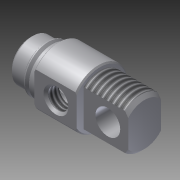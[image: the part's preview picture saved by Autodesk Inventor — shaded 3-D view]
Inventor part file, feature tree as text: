
AUTODESK INVENTOR PART (.ipt)
format: ipt  version: 2012 (Build 160160000, 160)  size: 246,784 bytes
history: native  units: in
note: dims shown in document units (in); Inventor stores cm internally (conversion verified against a paired STEP export)
features: other x126, sketch x8, revolve x3, extrude x3, hole x2, thread x1
ambient origin geometry x8: Origin, YZ Plane, XZ Plane, XY Plane, X Axis, Y Axis, Z Axis, Center Point
bodies: Solid1 (feature_tree)
feature tree (143):
  revolve  "Revolution1"  Angle=360.0deg
  revolve  "Revolution2"  [1 undecoded]
  thread  "Thread1"  [1 undecoded]
  extrude  "Extrusion1"  TaperAngle=360.0deg  [1 undecoded]
  extrude  "Extrusion2"  [1 undecoded]
  hole  "Drilling 1"  [1 undecoded]
  hole  "Drilling 2"  [1 undecoded]
  revolve  "Revolution3"  [1 undecoded]
  extrude  "Extrusion3"  [1 undecoded]
  other  "to_tube_XY"
  other  "to_tube_YZ"
  other  "to_tube_ZX"
  other  "to_tube_X"
  other  "to_tube_Y"
  other  "to_tube_Z"
  other  "to_tube_Center"
  other  "to_nut_XY"
  other  "to_nut_YZ"
  other  "to_nut_ZX"
  other  "to_nut_X"
  other  "to_nut_Y"
  other  "to_nut_Z"
  other  "to_nut_Center"
  other  "lovra1_XY"
  other  "lovra1_YZ"
  other  "lovra1_ZX"
  other  "lovra1_X"
  other  "lovra1_Y"
  other  "lovra1_Z"
  other  "lovra1_Center"
  other  "lovra2_XY"
  other  "lovra2_YZ"
  other  "lovra2_ZX"
  other  "lovra2_X"
  other  "lovra2_Y"
  other  "lovra2_Z"
  other  "lovra2_Center"
  other  "lovra3_XY"
  other  "lovra3_YZ"
  other  "lovra3_ZX"
  other  "lovra3_X"
  other  "lovra3_Y"
  other  "lovra3_Z"
  other  "lovra3_Center"
  other  "to_pin_XY"
  other  "to_pin_YZ"
  other  "to_pin_ZX"
  other  "to_pin_X"
  other  "to_pin_Y"
  other  "to_pin_Z"
  other  "to_pin_Center"
  other  "olen_XY"
  other  "olen_YZ"
  other  "olen_ZX"
  other  "olen_X"
  other  "olen_Y"
  other  "olen_Z"
  other  "olen_Center"
  other  "thd1_XY"
  other  "thd1_YZ"
  other  "thd1_ZX"
  other  "thd1_X"
  other  "thd1_Y"
  other  "thd1_Z"
  other  "thd1_Center"
  other  "p1_XY"
  other  "p1_YZ"
  other  "p1_ZX"
  other  "p1_X"
  other  "p1_Y"
  other  "p1_Z"
  other  "p1_Center"
  other  "thd2_XY"
  other  "thd2_YZ"
  other  "thd2_ZX"
  other  "thd2_X"
  other  "thd2_Y"
  other  "thd2_Z"
  other  "thd2_Center"
  other  "p2_XY"
  other  "p2_YZ"
  other  "p2_ZX"
  other  "p2_X"
  other  "p2_Y"
  other  "p2_Z"
  other  "p2_Center"
  other  "port2_XY"
  other  "port2_YZ"
  other  "port2_ZX"
  other  "port2_X"
  other  "port2_Y"
  other  "port2_Z"
  other  "port2_Center"
  other  "port_XY"
  other  "port_YZ"
  other  "port_ZX"
  other  "port_X"
  other  "port_Y"
  other  "port_Z"
  other  "port_Center"
  other  "1_XY"
  other  "1_YZ"
  other  "1_ZX"
  other  "1_X"
  other  "1_Y"
  other  "1_Z"
  other  "1_Center"
  other  "lovra21_XY"
  other  "lovra21_YZ"
  other  "lovra21_ZX"
  other  "lovra21_X"
  other  "lovra21_Y"
  other  "lovra21_Z"
  other  "lovra21_Center"
  other  "lovra22_XY"
  other  "lovra22_YZ"
  other  "lovra22_ZX"
  other  "lovra22_X"
  other  "lovra22_Y"
  other  "lovra22_Z"
  other  "lovra22_Center"
  other  "to_screw_XY"
  other  "to_screw_YZ"
  other  "to_screw_ZX"
  other  "to_screw_X"
  other  "to_screw_Y"
  other  "to_screw_Z"
  other  "to_screw_Center"
  other  "to_mounting_bracket_XY"
  other  "to_mounting_bracket_YZ"
  other  "to_mounting_bracket_ZX"
  other  "to_mounting_bracket_X"
  other  "to_mounting_bracket_Y"
  other  "to_mounting_bracket_Z"
  other  "to_mounting_bracket_Center"
  sketch  "Sketch_8"  dims[d8=0.1562in d9=0.75in d10=0.375in d11=0.25in d12=0.5635in d13=0.485in d14=120.0deg]
  sketch  "Sketch_14"  dims[d23=0.375in d24=0.0in]
  sketch  "Sketch_9"  dims[d15=0.156in d16=0.1004in d17=0.19in d18=0.25in d19=90.0deg d20=0.1785in d21=0.0in d22=360.0deg]
  sketch  "Sketch_44"
  sketch  "Sketch5"  dims[d0=360.0deg d1=360.0deg]
  sketch  "Sketch6"  dims[d2=0.3167in d3=0.0in d4=0.3415in d5=0.0in d6=0.323in d7=0.0in]
  sketch  "Sketch_24"
  sketch  "Sketch_43"
note: 8 required parameter values undecoded (feature->parameter linkage not recoverable at this tier; creation-order binding heuristic only, values carry confidence <= 0.55)